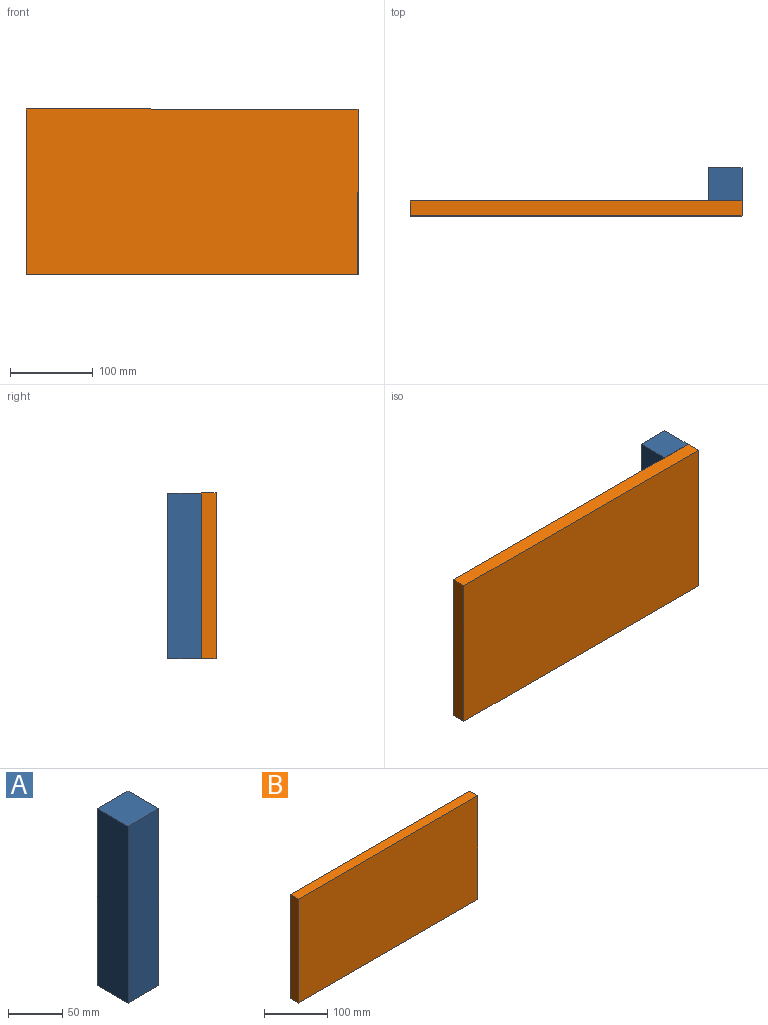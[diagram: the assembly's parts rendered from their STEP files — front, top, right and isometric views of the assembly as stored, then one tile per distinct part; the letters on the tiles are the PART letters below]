
ASSEMBLY  parts=2 mates=1
PART A: 6 faces, bbox 40x40x200 mm
  f0: plane 40x40mm, normal (0,0,1), area 1600mm2, adj f1,f3,f4,f5
  f1: plane 200x40mm, normal (-1,0,0), area 8000mm2, adj f0,f2,f4,f5
  f2: plane 40x40mm, normal (0,0,-1), area 1600mm2, adj f1,f3,f4,f5
  f3: plane 200x40mm, normal (1,0,0), area 8000mm2, adj f0,f2,f4,f5
  f4: plane 200x40mm, normal (0,-1,0), area 8000mm2, adj f0,f1,f2,f3
  f5: plane 200x40mm, normal (0,1,0), area 8000mm2, adj f0,f1,f2,f3
PART B: 6 faces, bbox 400x18x200 mm
  f0: plane 400x18mm, normal (0,0,-1), area 7200mm2, adj f1,f3,f4,f5
  f1: plane 200x18mm, normal (1,0,0), area 3600mm2, adj f0,f2,f4,f5
  f2: plane 400x18mm, normal (0,0,1), area 7200mm2, adj f1,f3,f4,f5
  f3: plane 200x18mm, normal (-1,0,0), area 3600mm2, adj f0,f2,f4,f5
  f4: plane 400x200mm, normal (0,-1,0), area 80000mm2, adj f0,f1,f2,f3
  f5: plane 400x200mm, normal (0,1,0), area 80000mm2, adj f0,f1,f2,f3
PLACE A t=(156.78,127.69,-32.77)mm
PLACE B t=(-23.22,87.69,-32.77)mm
MATE fastened B.f2 <-> A.f0  axis (0,0,1) through (176.78,87.69,67.23)mm
